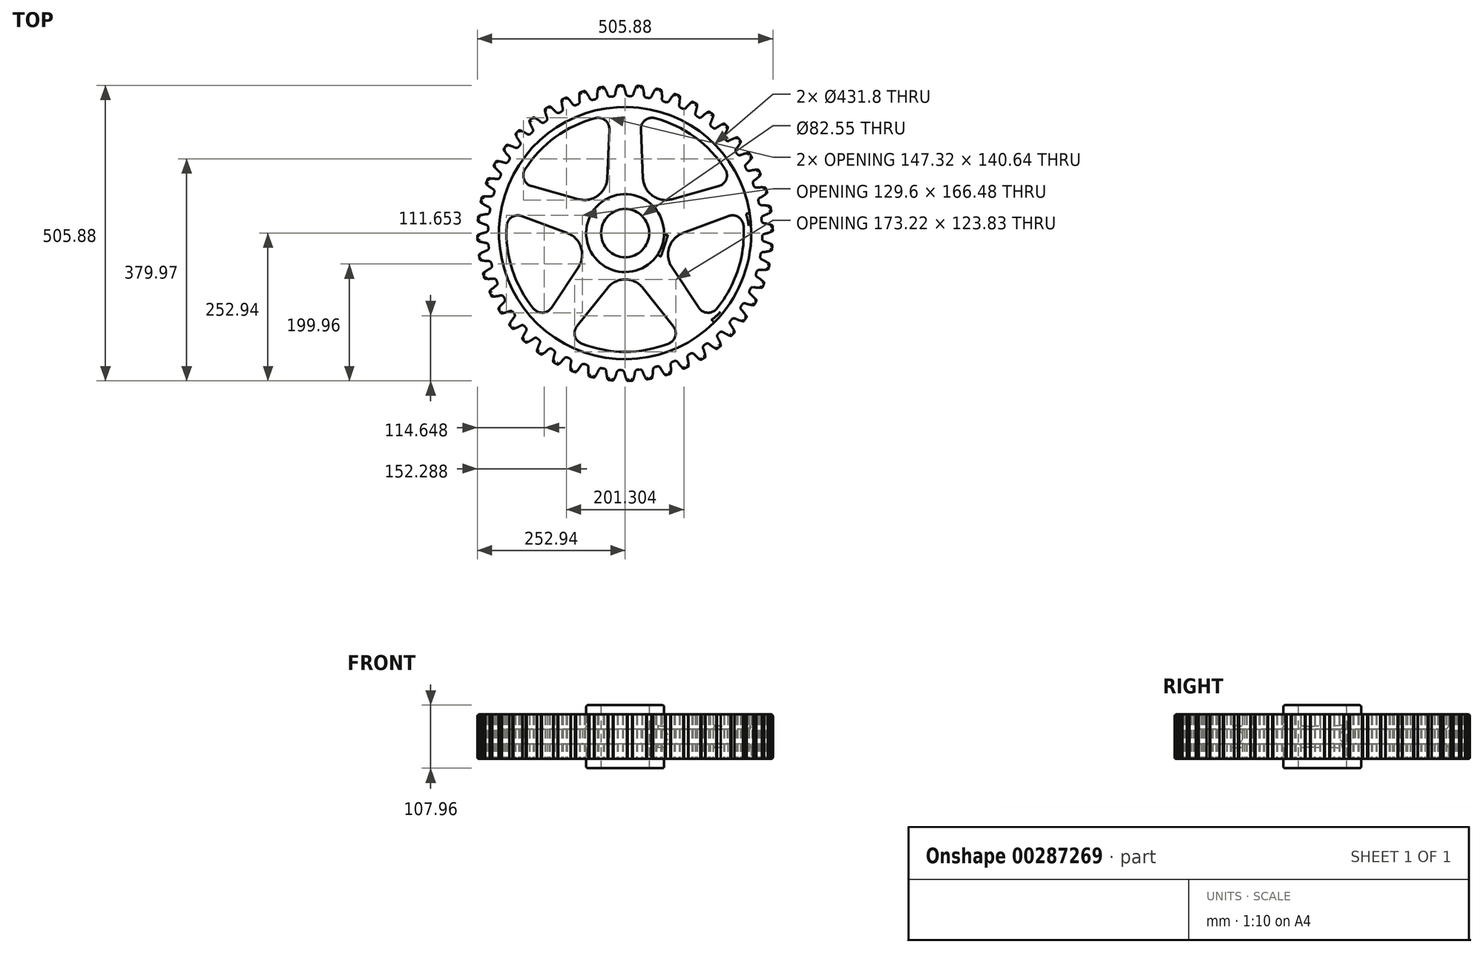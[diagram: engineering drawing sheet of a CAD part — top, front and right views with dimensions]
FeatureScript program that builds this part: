
annotation { "Feature Type Name" : "Feature", "Feature Type Description" : "" }
export const myFeature = defineFeature(function(context is Context, id is Id, definition is map)
    precondition{}
    {
        {
            var Q0;
            Q0=qCreatedBy(makeId("Top.planeOp"),FACE);
            var sketch = newSketch(context, id + "F0", { "sketchPlane" : qUnion([Q0])});
            skCircle(sketch, "E0", {"center": v(0, 0) * mm, "radius": 215.9 * mm});
            skCircle(sketch, "E1", {"center": v(0, 0) * mm, "radius": 233.95 * mm, "construction": true});
            skCircle(sketch, "E2", {"center": v(0, 0) * mm, "radius": 243.84 * mm, "construction": true});
            skLineSegment(sketch, "E3", {"start": v(0, 0) * mm, "end": v(0, 296.8) * mm, "construction": true});
            skLineSegment(sketch, "E4", {"start": v(0, 0) * mm, "end": v(-9.72, 296.8) * mm, "construction": true});
            skLineSegment(sketch, "E5", {"start": v(0, 243.84) * mm, "end": v(-159.16, 238.63) * mm, "construction": true});
            skLineSegment(sketch, "E6", {"start": v(0, 243.84) * mm, "end": v(-157.2, 197.65) * mm, "construction": true});
            skArc(sketch, "E7", {"start": v(-21.3, 233.73) * mm, "mid": v(7.68, -234.57) * mm, "end": v(5.96, 234.62) * mm});
            skCircle(sketch, "E8", {"center": v(0, 243.84) * mm, "radius": 60.96 * mm, "construction": true});
            skArc(sketch, "E9", {"start": v(1.3, 238.54) * mm, "mid": v(-0.65, 245.9) * mm, "end": v(-3.5, 252.96) * mm});
            skArc(sketch, "E10.MirrorCS", {"start": v(-16.9, 237.95) * mm, "mid": v(-15.44, 245.42) * mm, "end": v(-13.06, 252.65) * mm});
            skArc(sketch, "E11.trimOffspring", {"start": v(-3.5, 252.96) * mm, "mid": v(-8.28, 252.85) * mm, "end": v(-13.06, 252.65) * mm});
            skPoint(sketch, "E12.visualSharp", {"position": v(-17.29, 234.06) * mm});
            skArc(sketch, "E12.filletArc", {"start": v(-21.3, 233.73) * mm, "mid": v(-18.36, 235.07) * mm, "end": v(-16.9, 237.95) * mm});
            skPoint(sketch, "E13.visualSharp", {"position": v(1.94, 234.69) * mm});
            skArc(sketch, "E13.filletArc", {"start": v(1.3, 238.54) * mm, "mid": v(2.94, 235.77) * mm, "end": v(5.96, 234.62) * mm});
            skCircle(sketch, "E14", {"center": v(0, 0) * mm, "radius": 41.28 * mm});
            skCircle(sketch, "E15", {"center": v(0, 0) * mm, "radius": 66.68 * mm});
            skSolve(sketch);
        }
        {
            var Q0;
            Q0 = qSketchRegion(id + "F0", true);
            extrude(context, id + "F1", {"entities" : qUnion([Q0]), "depth" : 76.2 * mm, "symmetric" : true});
        }
        {
            var Q0;
            Q0=makeQuery(id+"F1.opExtrude","SWEPT_EDGE",EDGE,{"disambiguationData":[OSD([sQuery(id+"F0.wireOp",EDGE,"a425b38e-6d31-48f0-aded-03e86b7642bf0.MirrorCS"),sQuery(id+"F0.wireOp",EDGE,"e7ba85ad-8bea-4f75-aefd-55836ceef68a.trimOffspring")])]});
            var Q1;
            Q1=makeQuery(id+"F1.opExtrude","SWEPT_EDGE",EDGE,{"disambiguationData":[OSD([sQuery(id+"F0.wireOp",EDGE,"58a562a5-3fed-4315-ace1-1cd0f613343d.trimOffspring"),sQuery(id+"F0.wireOp",EDGE,"e7ba85ad-8bea-4f75-aefd-55836ceef68a.trimOffspring")])]});
            var Q2;
            Q2=makeQuery(id+"F1.opExtrude","SWEPT_EDGE",EDGE,{"disambiguationData":[OSD([sQuery(id+"F0.wireOp",EDGE,"E10.MirrorCS"),sQuery(id+"F0.wireOp",EDGE,"E11.trimOffspring")])]});
            var Q3;
            Q3=makeQuery(id+"F1.opExtrude","SWEPT_EDGE",EDGE,{"disambiguationData":[OSD([sQuery(id+"F0.wireOp",EDGE,"E9"),sQuery(id+"F0.wireOp",EDGE,"E11.trimOffspring")])]});
            chamfer(context, id + "F2", {"entities" : qUnion([Q0, Q1, Q2, Q3]), "width" : 1.59 * mm, "tangentPropagation" : true});
        }
        {
            var Q0;
            Q0=makeQuery(id+"F0.imprint","IMPRINT",FACE,{"disambiguationData":[TD([[makeQuery(id+"F0.imprint","IMPRINT",EDGE,{"derivedFrom":sQuery(id+"F0.wireOp",EDGE,"E14")}),-1.0]])]});
            extrude(context, id + "F3", {"entities" : qUnion([Q0]), "depth" : 107.95 * mm, "symmetric" : true});
        }
        {
            var Q0;
            Q0=makeQuery(id+"F1.opExtrude","SWEPT_BODY",BODY,{"disambiguationData":[OSD([sQuery(id+"F0.wireOp",EDGE,"E0"),sQuery(id+"F0.wireOp",EDGE,"E7"),sQuery(id+"F0.wireOp",EDGE,"E9"),sQuery(id+"F0.wireOp",EDGE,"E10.MirrorCS"),sQuery(id+"F0.wireOp",EDGE,"E11.trimOffspring"),sQuery(id+"F0.wireOp",EDGE,"E12.filletArc"),sQuery(id+"F0.wireOp",EDGE,"E13.filletArc")])]});
            var Q1;
            Q1=makeQuery(id+"F3.opExtrude","SWEPT_FACE",FACE,{"disambiguationData":[OSD([sQuery(id+"F0.wireOp",EDGE,"E15")])]});
            circularPattern(context, id + "F4", {"operationType" : NewBodyOperationType.ADD, "entities" : qUnion([Q0]), "axis" : qUnion([Q1]), "angle" : 360 * degree, "instanceCount" : 48, "equalSpace" : true});
        }
        {
            var Q0;
            Q0=qCreatedBy(makeId("Front.planeOp"),FACE);
            var sketch = newSketch(context, id + "F5", { "sketchPlane" : qUnion([Q0])});
            skLineSegment(sketch, "E16", {"start": v(-215.9, -12.7) * mm, "end": v(-215.9, 12.7) * mm});
            skPoint(sketch, "E17.orphan", {"position": v(-215.9, 38.1) * mm});
            skPoint(sketch, "E18.orphan", {"position": v(-215.9, -38.1) * mm});
            skLineSegment(sketch, "E19", {"start": v(-66.68, -12.7) * mm, "end": v(-66.68, 12.7) * mm});
            skLineSegment(sketch, "E20.bottom", {"start": v(-66.68, -12.7) * mm, "end": v(-79.38, -12.7) * mm});
            skLineSegment(sketch, "E20.top", {"start": v(-66.68, 12.7) * mm, "end": v(-79.38, 12.7) * mm});
            skLineSegment(sketch, "E20.right", {"start": v(-79.38, -12.7) * mm, "end": v(-79.38, 12.7) * mm});
            skPoint(sketch, "E20.middle", {"position": v(-66.68, 0) * mm});
            skPoint(sketch, "E20.left.end.orphan", {"position": v(-53.98, 12.7) * mm});
            skPoint(sketch, "E20.left.start.orphan", {"position": v(-53.98, -12.7) * mm});
            skPoint(sketch, "E21.orphan", {"position": v(-66.68, -53.98) * mm});
            skPoint(sketch, "E22.orphan", {"position": v(-66.68, 53.98) * mm});
            skLineSegment(sketch, "E23.bottom", {"start": v(-203.2, 12.7) * mm, "end": v(-215.9, 12.7) * mm});
            skLineSegment(sketch, "E23.top", {"start": v(-203.2, -12.7) * mm, "end": v(-215.9, -12.7) * mm});
            skLineSegment(sketch, "E23.left", {"start": v(-203.2, 12.7) * mm, "end": v(-203.2, -12.7) * mm});
            skPoint(sketch, "E23.middle", {"position": v(-215.9, 0) * mm});
            skPoint(sketch, "E23.right.start.orphan", {"position": v(-228.6, 12.7) * mm});
            skPoint(sketch, "E24.orphan", {"position": v(-228.6, -12.7) * mm});
            skSolve(sketch);
        }
        {
            var Q0;
            Q0=makeQuery(id+"F5.imprint","IMPRINT",FACE,{"disambiguationData":[TD([[makeQuery(id+"F5.imprint","IMPRINT",EDGE,{"derivedFrom":sQuery(id+"F5.wireOp",EDGE,"E16")}),-1.0]])]});
            var Q1;
            Q1=makeQuery(id+"F3.opExtrude","SWEPT_FACE",FACE,{"disambiguationData":[OSD([sQuery(id+"F0.wireOp",EDGE,"E14")])]});
            revolve(context, id + "F6", {"operationType" : NewBodyOperationType.ADD, "entities" : qUnion([Q0]), "axis" : qUnion([Q1]), "revolveType" : RevolveType.FULL});
        }
        {
            var Q0;
            Q0=makeQuery(id+"F5.imprint","IMPRINT",FACE,{"disambiguationData":[TD([[makeQuery(id+"F5.imprint","IMPRINT",EDGE,{"derivedFrom":sQuery(id+"F5.wireOp",EDGE,"E19")}),1.0]])]});
            var Q1;
            Q1=makeQuery(id+"F3.opExtrude","SWEPT_FACE",FACE,{"disambiguationData":[OSD([sQuery(id+"F0.wireOp",EDGE,"E14")])]});
            revolve(context, id + "F7", {"operationType" : NewBodyOperationType.ADD, "entities" : qUnion([Q0]), "axis" : qUnion([Q1]), "revolveType" : RevolveType.FULL});
        }
        {
            var Q0;
            Q0=qCreatedBy(makeId("Top.planeOp"),FACE);
            var sketch = newSketch(context, id + "F8", { "sketchPlane" : qUnion([Q0])});
            skCircle(sketch, "E25.0", {"center": v(0, 0) * mm, "radius": 215.9 * mm});
            skCircle(sketch, "E26.0", {"center": v(0, 0) * mm, "radius": 66.68 * mm});
            skLineSegment(sketch, "E27", {"start": v(0, 66.68) * mm, "end": v(0, 215.9) * mm});
            skLineSegment(sketch, "E28", {"start": v(25.4, 214.4) * mm, "end": v(32.14, 58.42) * mm});
            skLineSegment(sketch, "E29.MirrorCS", {"start": v(-25.4, 214.4) * mm, "end": v(-32.14, 58.42) * mm});
            skSolve(sketch);
        }
        {
            var Q0;
            {var subQ0=sQuery(id+"F8.wireOp",EDGE,"E27");Q0=makeQuery(id+"F8.imprint","IMPRINT",FACE,{"disambiguationData":[TD([[makeQuery(id+"F8.imprint","IMPRINT",EDGE,{"derivedFrom":subQ0}),1.0]])]});}
            var Q1;
            {var subQ0=sQuery(id+"F8.wireOp",EDGE,"E27");Q1=makeQuery(id+"F8.imprint","IMPRINT",FACE,{"disambiguationData":[TD([[makeQuery(id+"F8.imprint","IMPRINT",EDGE,{"derivedFrom":subQ0}),-1.0]])]});}
            extrude(context, id + "F9", {"entities" : qUnion([Q0, Q1]), "depth" : 25.4 * mm, "symmetric" : true});
        }
        {
            var Q0;
            Q0=makeQuery(id+"F9.opExtrude","SWEPT_BODY",BODY,{"disambiguationData":[OSD([sQuery(id+"F8.wireOp",EDGE,"E25.0"),sQuery(id+"F8.wireOp",EDGE,"E26.0"),sQuery(id+"F8.wireOp",EDGE,"E28"),sQuery(id+"F8.wireOp",EDGE,"E29.MirrorCS")])]});
            var Q1;
            Q1=makeQuery(id+"F3.opExtrude","SWEPT_FACE",FACE,{"disambiguationData":[OSD([sQuery(id+"F0.wireOp",EDGE,"E14")])]});
            circularPattern(context, id + "F10", {"entities" : qUnion([Q0]), "axis" : qUnion([Q1]), "angle" : 360 * degree, "instanceCount" : 5, "equalSpace" : true});
        }
        {
            var Q0;
            Q0=makeQuery(id+"F10.opPattern","COPY",BODY,{"derivedFrom":makeQuery(id+"F9.opExtrude","SWEPT_BODY",BODY,{"disambiguationData":[OSD([sQuery(id+"F8.wireOp",EDGE,"E25.0"),sQuery(id+"F8.wireOp",EDGE,"E26.0"),sQuery(id+"F8.wireOp",EDGE,"E28"),sQuery(id+"F8.wireOp",EDGE,"E29.MirrorCS")])]}),"instanceName":"2"});
            var Q1;
            Q1=makeQuery(id+"F10.opPattern","COPY",BODY,{"derivedFrom":makeQuery(id+"F9.opExtrude","SWEPT_BODY",BODY,{"disambiguationData":[OSD([sQuery(id+"F8.wireOp",EDGE,"E25.0"),sQuery(id+"F8.wireOp",EDGE,"E26.0"),sQuery(id+"F8.wireOp",EDGE,"E28"),sQuery(id+"F8.wireOp",EDGE,"E29.MirrorCS")])]}),"instanceName":"1"});
            var Q2;
            Q2=makeQuery(id+"F10.opPattern","COPY",BODY,{"derivedFrom":makeQuery(id+"F9.opExtrude","SWEPT_BODY",BODY,{"disambiguationData":[OSD([sQuery(id+"F8.wireOp",EDGE,"E25.0"),sQuery(id+"F8.wireOp",EDGE,"E26.0"),sQuery(id+"F8.wireOp",EDGE,"E28"),sQuery(id+"F8.wireOp",EDGE,"E29.MirrorCS")])]}),"instanceName":"4"});
            var Q3;
            Q3=makeQuery(id+"F10.opPattern","COPY",BODY,{"derivedFrom":makeQuery(id+"F9.opExtrude","SWEPT_BODY",BODY,{"disambiguationData":[OSD([sQuery(id+"F8.wireOp",EDGE,"E25.0"),sQuery(id+"F8.wireOp",EDGE,"E26.0"),sQuery(id+"F8.wireOp",EDGE,"E28"),sQuery(id+"F8.wireOp",EDGE,"E29.MirrorCS")])]}),"instanceName":"3"});
            var Q4;
            Q4=makeQuery(id+"F9.opExtrude","SWEPT_BODY",BODY,{"disambiguationData":[OSD([sQuery(id+"F8.wireOp",EDGE,"E25.0"),sQuery(id+"F8.wireOp",EDGE,"E26.0"),sQuery(id+"F8.wireOp",EDGE,"E28"),sQuery(id+"F8.wireOp",EDGE,"E29.MirrorCS")])]});
            var Q5;
            Q5=makeQuery(id+"F3.opExtrude","SWEPT_BODY",BODY,{"disambiguationData":[OSD([sQuery(id+"F0.wireOp",EDGE,"E14"),sQuery(id+"F0.wireOp",EDGE,"E15")])]});
            var Q6;
            Q6=makeQuery(id+"F1.opExtrude","SWEPT_BODY",BODY,{"disambiguationData":[OSD([sQuery(id+"F0.wireOp",EDGE,"E0"),sQuery(id+"F0.wireOp",EDGE,"E7"),sQuery(id+"F0.wireOp",EDGE,"E9"),sQuery(id+"F0.wireOp",EDGE,"E10.MirrorCS"),sQuery(id+"F0.wireOp",EDGE,"E11.trimOffspring"),sQuery(id+"F0.wireOp",EDGE,"E12.filletArc"),sQuery(id+"F0.wireOp",EDGE,"E13.filletArc")])]});
            booleanBodies(context, id + "F11", {"operationType" : BooleanOperationType.UNION, "tools" : qUnion([Q0, Q1, Q2, Q3, Q4, Q5, Q6])});
        }
        {
            var Q0;
            Q0=makeQuery(id+"F11.opBoolean","INTERSECT",EDGE,{"derivedFrom":[makeQuery(id+"F7.opRevolve","SWEPT_FACE",FACE,{"disambiguationData":[OSD([sQuery(id+"F5.wireOp",EDGE,"E20.right")])]}),makeQuery(id+"F9.opExtrude","SWEPT_FACE",FACE,{"disambiguationData":[OSD([sQuery(id+"F8.wireOp",EDGE,"E28")])]})]});
            var Q1;
            Q1=makeQuery(id+"F11.opBoolean","INTERSECT",EDGE,{"derivedFrom":[makeQuery(id+"F7.opRevolve","SWEPT_FACE",FACE,{"disambiguationData":[OSD([sQuery(id+"F5.wireOp",EDGE,"E20.right")])]}),makeQuery(id+"F10.opPattern","COPY",FACE,{"derivedFrom":makeQuery(id+"F9.opExtrude","SWEPT_FACE",FACE,{"disambiguationData":[OSD([sQuery(id+"F8.wireOp",EDGE,"E29.MirrorCS")])]}),"instanceName":"4"})]});
            var Q2;
            Q2=makeQuery(id+"F11.opBoolean","INTERSECT",EDGE,{"derivedFrom":[makeQuery(id+"F7.opRevolve","SWEPT_FACE",FACE,{"disambiguationData":[OSD([sQuery(id+"F5.wireOp",EDGE,"E20.right")])]}),makeQuery(id+"F10.opPattern","COPY",FACE,{"derivedFrom":makeQuery(id+"F9.opExtrude","SWEPT_FACE",FACE,{"disambiguationData":[OSD([sQuery(id+"F8.wireOp",EDGE,"E28")])]}),"instanceName":"1"})]});
            var Q3;
            Q3=makeQuery(id+"F11.opBoolean","INTERSECT",EDGE,{"derivedFrom":[makeQuery(id+"F7.opRevolve","SWEPT_FACE",FACE,{"disambiguationData":[OSD([sQuery(id+"F5.wireOp",EDGE,"E20.right")])]}),makeQuery(id+"F9.opExtrude","SWEPT_FACE",FACE,{"disambiguationData":[OSD([sQuery(id+"F8.wireOp",EDGE,"E29.MirrorCS")])]})]});
            var Q4;
            Q4=makeQuery(id+"F11.opBoolean","INTERSECT",EDGE,{"derivedFrom":[makeQuery(id+"F7.opRevolve","SWEPT_FACE",FACE,{"disambiguationData":[OSD([sQuery(id+"F5.wireOp",EDGE,"E20.right")])]}),makeQuery(id+"F10.opPattern","COPY",FACE,{"derivedFrom":makeQuery(id+"F9.opExtrude","SWEPT_FACE",FACE,{"disambiguationData":[OSD([sQuery(id+"F8.wireOp",EDGE,"E29.MirrorCS")])]}),"instanceName":"1"})]});
            var Q5;
            Q5=makeQuery(id+"F11.opBoolean","INTERSECT",EDGE,{"derivedFrom":[makeQuery(id+"F7.opRevolve","SWEPT_FACE",FACE,{"disambiguationData":[OSD([sQuery(id+"F5.wireOp",EDGE,"E20.right")])]}),makeQuery(id+"F10.opPattern","COPY",FACE,{"derivedFrom":makeQuery(id+"F9.opExtrude","SWEPT_FACE",FACE,{"disambiguationData":[OSD([sQuery(id+"F8.wireOp",EDGE,"E28")])]}),"instanceName":"2"})]});
            var Q6;
            Q6=makeQuery(id+"F11.opBoolean","INTERSECT",EDGE,{"derivedFrom":[makeQuery(id+"F7.opRevolve","SWEPT_FACE",FACE,{"disambiguationData":[OSD([sQuery(id+"F5.wireOp",EDGE,"E20.right")])]}),makeQuery(id+"F10.opPattern","COPY",FACE,{"derivedFrom":makeQuery(id+"F9.opExtrude","SWEPT_FACE",FACE,{"disambiguationData":[OSD([sQuery(id+"F8.wireOp",EDGE,"E29.MirrorCS")])]}),"instanceName":"2"})]});
            var Q7;
            Q7=makeQuery(id+"F11.opBoolean","INTERSECT",EDGE,{"derivedFrom":[makeQuery(id+"F7.opRevolve","SWEPT_FACE",FACE,{"disambiguationData":[OSD([sQuery(id+"F5.wireOp",EDGE,"E20.right")])]}),makeQuery(id+"F10.opPattern","COPY",FACE,{"derivedFrom":makeQuery(id+"F9.opExtrude","SWEPT_FACE",FACE,{"disambiguationData":[OSD([sQuery(id+"F8.wireOp",EDGE,"E28")])]}),"instanceName":"3"})]});
            var Q8;
            Q8=makeQuery(id+"F11.opBoolean","INTERSECT",EDGE,{"derivedFrom":[makeQuery(id+"F7.opRevolve","SWEPT_FACE",FACE,{"disambiguationData":[OSD([sQuery(id+"F5.wireOp",EDGE,"E20.right")])]}),makeQuery(id+"F10.opPattern","COPY",FACE,{"derivedFrom":makeQuery(id+"F9.opExtrude","SWEPT_FACE",FACE,{"disambiguationData":[OSD([sQuery(id+"F8.wireOp",EDGE,"E29.MirrorCS")])]}),"instanceName":"3"})]});
            var Q9;
            Q9=makeQuery(id+"F11.opBoolean","INTERSECT",EDGE,{"derivedFrom":[makeQuery(id+"F7.opRevolve","SWEPT_FACE",FACE,{"disambiguationData":[OSD([sQuery(id+"F5.wireOp",EDGE,"E20.right")])]}),makeQuery(id+"F10.opPattern","COPY",FACE,{"derivedFrom":makeQuery(id+"F9.opExtrude","SWEPT_FACE",FACE,{"disambiguationData":[OSD([sQuery(id+"F8.wireOp",EDGE,"E28")])]}),"instanceName":"4"})]});
            fillet(context, id + "F12", {"entities" : qUnion([Q0, Q1, Q2, Q3, Q4, Q5, Q6, Q7, Q8, Q9]), "radius" : 38.1 * mm, "tangentPropagation" : true, "allowEdgeOverflow" : false});
        }
        {
            var Q0;
            Q0=makeQuery(id+"F11.opBoolean","INTERSECT",EDGE,{"derivedFrom":[makeQuery(id+"F6.opRevolve","SWEPT_FACE",FACE,{"disambiguationData":[OSD([sQuery(id+"F5.wireOp",EDGE,"E23.left")])]}),makeQuery(id+"F10.opPattern","COPY",FACE,{"derivedFrom":makeQuery(id+"F9.opExtrude","SWEPT_FACE",FACE,{"disambiguationData":[OSD([sQuery(id+"F8.wireOp",EDGE,"E28")])]}),"instanceName":"2"})]});
            var Q1;
            Q1=makeQuery(id+"F11.opBoolean","INTERSECT",EDGE,{"derivedFrom":[makeQuery(id+"F6.opRevolve","SWEPT_FACE",FACE,{"disambiguationData":[OSD([sQuery(id+"F5.wireOp",EDGE,"E23.left")])]}),makeQuery(id+"F10.opPattern","COPY",FACE,{"derivedFrom":makeQuery(id+"F9.opExtrude","SWEPT_FACE",FACE,{"disambiguationData":[OSD([sQuery(id+"F8.wireOp",EDGE,"E29.MirrorCS")])]}),"instanceName":"2"})]});
            var Q2;
            Q2=makeQuery(id+"F11.opBoolean","INTERSECT",EDGE,{"derivedFrom":[makeQuery(id+"F6.opRevolve","SWEPT_FACE",FACE,{"disambiguationData":[OSD([sQuery(id+"F5.wireOp",EDGE,"E23.left")])]}),makeQuery(id+"F10.opPattern","COPY",FACE,{"derivedFrom":makeQuery(id+"F9.opExtrude","SWEPT_FACE",FACE,{"disambiguationData":[OSD([sQuery(id+"F8.wireOp",EDGE,"E28")])]}),"instanceName":"3"})]});
            var Q3;
            Q3=makeQuery(id+"F11.opBoolean","INTERSECT",EDGE,{"derivedFrom":[makeQuery(id+"F6.opRevolve","SWEPT_FACE",FACE,{"disambiguationData":[OSD([sQuery(id+"F5.wireOp",EDGE,"E23.left")])]}),makeQuery(id+"F10.opPattern","COPY",FACE,{"derivedFrom":makeQuery(id+"F9.opExtrude","SWEPT_FACE",FACE,{"disambiguationData":[OSD([sQuery(id+"F8.wireOp",EDGE,"E29.MirrorCS")])]}),"instanceName":"3"})]});
            var Q4;
            Q4=makeQuery(id+"F11.opBoolean","INTERSECT",EDGE,{"derivedFrom":[makeQuery(id+"F6.opRevolve","SWEPT_FACE",FACE,{"disambiguationData":[OSD([sQuery(id+"F5.wireOp",EDGE,"E23.left")])]}),makeQuery(id+"F10.opPattern","COPY",FACE,{"derivedFrom":makeQuery(id+"F9.opExtrude","SWEPT_FACE",FACE,{"disambiguationData":[OSD([sQuery(id+"F8.wireOp",EDGE,"E29.MirrorCS")])]}),"instanceName":"1"})]});
            var Q5;
            Q5=makeQuery(id+"F11.opBoolean","INTERSECT",EDGE,{"derivedFrom":[makeQuery(id+"F6.opRevolve","SWEPT_FACE",FACE,{"disambiguationData":[OSD([sQuery(id+"F5.wireOp",EDGE,"E23.left")])]}),makeQuery(id+"F10.opPattern","COPY",FACE,{"derivedFrom":makeQuery(id+"F9.opExtrude","SWEPT_FACE",FACE,{"disambiguationData":[OSD([sQuery(id+"F8.wireOp",EDGE,"E28")])]}),"instanceName":"1"})]});
            var Q6;
            Q6=makeQuery(id+"F11.opBoolean","INTERSECT",EDGE,{"derivedFrom":[makeQuery(id+"F6.opRevolve","SWEPT_FACE",FACE,{"disambiguationData":[OSD([sQuery(id+"F5.wireOp",EDGE,"E23.left")])]}),makeQuery(id+"F10.opPattern","COPY",FACE,{"derivedFrom":makeQuery(id+"F9.opExtrude","SWEPT_FACE",FACE,{"disambiguationData":[OSD([sQuery(id+"F8.wireOp",EDGE,"E28")])]}),"instanceName":"4"})]});
            var Q7;
            Q7=makeQuery(id+"F11.opBoolean","INTERSECT",EDGE,{"derivedFrom":[makeQuery(id+"F6.opRevolve","SWEPT_FACE",FACE,{"disambiguationData":[OSD([sQuery(id+"F5.wireOp",EDGE,"E23.left")])]}),makeQuery(id+"F10.opPattern","COPY",FACE,{"derivedFrom":makeQuery(id+"F9.opExtrude","SWEPT_FACE",FACE,{"disambiguationData":[OSD([sQuery(id+"F8.wireOp",EDGE,"E29.MirrorCS")])]}),"instanceName":"4"})]});
            var Q8;
            Q8=makeQuery(id+"F11.opBoolean","INTERSECT",EDGE,{"derivedFrom":[makeQuery(id+"F6.opRevolve","SWEPT_FACE",FACE,{"disambiguationData":[OSD([sQuery(id+"F5.wireOp",EDGE,"E23.left")])]}),makeQuery(id+"F9.opExtrude","SWEPT_FACE",FACE,{"disambiguationData":[OSD([sQuery(id+"F8.wireOp",EDGE,"E28")])]})]});
            var Q9;
            Q9=makeQuery(id+"F11.opBoolean","INTERSECT",EDGE,{"derivedFrom":[makeQuery(id+"F6.opRevolve","SWEPT_FACE",FACE,{"disambiguationData":[OSD([sQuery(id+"F5.wireOp",EDGE,"E23.left")])]}),makeQuery(id+"F9.opExtrude","SWEPT_FACE",FACE,{"disambiguationData":[OSD([sQuery(id+"F8.wireOp",EDGE,"E29.MirrorCS")])]})]});
            fillet(context, id + "F13", {"entities" : qUnion([Q0, Q1, Q2, Q3, Q4, Q5, Q6, Q7, Q8, Q9]), "radius" : 19.05 * mm, "tangentPropagation" : true, "allowEdgeOverflow" : false});
        }
        {
            var Q0;
            {var subQ0=sQuery(id+"F8.wireOp",EDGE,"E29.MirrorCS");var subQ3=sQuery(id+"F5.wireOp",EDGE,"E23.left");var subQ4=sQuery(id+"F5.wireOp",EDGE,"E23.bottom");Q0=makeQuery(id+"F11.opBoolean","SPLIT",EDGE,{"disambiguationData":[TD([makeQuery(id+"F10.opPattern","COPY",FACE,{"derivedFrom":makeQuery(id+"F9.opExtrude","SWEPT_FACE",FACE,{"disambiguationData":[OSD([subQ0])]}),"instanceName":"2"})])],"derivedFrom":makeQuery(id+"F6.opRevolve","SWEPT_EDGE",EDGE,{"disambiguationData":[OSD([subQ4,subQ3])]})});}
            var Q1;
            {var subQ0=sQuery(id+"F8.wireOp",EDGE,"E29.MirrorCS");var subQ3=sQuery(id+"F5.wireOp",EDGE,"E23.left");var subQ4=sQuery(id+"F5.wireOp",EDGE,"E23.bottom");Q1=makeQuery(id+"F11.opBoolean","SPLIT",EDGE,{"disambiguationData":[TD([makeQuery(id+"F10.opPattern","COPY",FACE,{"derivedFrom":makeQuery(id+"F9.opExtrude","SWEPT_FACE",FACE,{"disambiguationData":[OSD([subQ0])]}),"instanceName":"1"})])],"derivedFrom":makeQuery(id+"F6.opRevolve","SWEPT_EDGE",EDGE,{"disambiguationData":[OSD([subQ4,subQ3])]})});}
            var Q2;
            {var subQ0=sQuery(id+"F8.wireOp",EDGE,"E29.MirrorCS");var subQ3=sQuery(id+"F5.wireOp",EDGE,"E23.left");var subQ4=sQuery(id+"F5.wireOp",EDGE,"E23.bottom");Q2=makeQuery(id+"F11.opBoolean","SPLIT",EDGE,{"disambiguationData":[TD([makeQuery(id+"F10.opPattern","COPY",FACE,{"derivedFrom":makeQuery(id+"F9.opExtrude","SWEPT_FACE",FACE,{"disambiguationData":[OSD([subQ0])]}),"instanceName":"3"})])],"derivedFrom":makeQuery(id+"F6.opRevolve","SWEPT_EDGE",EDGE,{"disambiguationData":[OSD([subQ4,subQ3])]})});}
            var Q3;
            {var subQ1=sQuery(id+"F8.wireOp",EDGE,"E28");var subQ3=sQuery(id+"F5.wireOp",EDGE,"E23.left");var subQ4=sQuery(id+"F5.wireOp",EDGE,"E23.bottom");Q3=makeQuery(id+"F11.opBoolean","SPLIT",EDGE,{"disambiguationData":[TD([makeQuery(id+"F9.opExtrude","SWEPT_FACE",FACE,{"disambiguationData":[OSD([subQ1])]})])],"derivedFrom":makeQuery(id+"F6.opRevolve","SWEPT_EDGE",EDGE,{"disambiguationData":[OSD([subQ4,subQ3])]})});}
            var Q4;
            {var subQ1=sQuery(id+"F8.wireOp",EDGE,"E29.MirrorCS");var subQ3=sQuery(id+"F5.wireOp",EDGE,"E23.left");var subQ4=sQuery(id+"F5.wireOp",EDGE,"E23.bottom");Q4=makeQuery(id+"F11.opBoolean","SPLIT",EDGE,{"disambiguationData":[TD([makeQuery(id+"F9.opExtrude","SWEPT_FACE",FACE,{"disambiguationData":[OSD([subQ1])]})])],"derivedFrom":makeQuery(id+"F6.opRevolve","SWEPT_EDGE",EDGE,{"disambiguationData":[OSD([subQ4,subQ3])]})});}
            var Q5;
            {var subQ0=sQuery(id+"F5.wireOp",EDGE,"E23.left");var subQ1=sQuery(id+"F8.wireOp",EDGE,"E29.MirrorCS");var subQ4=sQuery(id+"F5.wireOp",EDGE,"E23.top");Q5=makeQuery(id+"F11.opBoolean","SPLIT",EDGE,{"disambiguationData":[TD([makeQuery(id+"F9.opExtrude","SWEPT_FACE",FACE,{"disambiguationData":[OSD([subQ1])]})])],"derivedFrom":makeQuery(id+"F6.opRevolve","SWEPT_EDGE",EDGE,{"disambiguationData":[OSD([subQ4,subQ0])]})});}
            var Q6;
            {var subQ0=sQuery(id+"F5.wireOp",EDGE,"E23.left");var subQ2=sQuery(id+"F8.wireOp",EDGE,"E28");var subQ4=sQuery(id+"F5.wireOp",EDGE,"E23.top");Q6=makeQuery(id+"F11.opBoolean","SPLIT",EDGE,{"disambiguationData":[TD([makeQuery(id+"F9.opExtrude","SWEPT_FACE",FACE,{"disambiguationData":[OSD([subQ2])]})])],"derivedFrom":makeQuery(id+"F6.opRevolve","SWEPT_EDGE",EDGE,{"disambiguationData":[OSD([subQ4,subQ0])]})});}
            var Q7;
            {var subQ0=sQuery(id+"F5.wireOp",EDGE,"E23.left");var subQ1=sQuery(id+"F8.wireOp",EDGE,"E29.MirrorCS");var subQ4=sQuery(id+"F5.wireOp",EDGE,"E23.top");Q7=makeQuery(id+"F11.opBoolean","SPLIT",EDGE,{"disambiguationData":[TD([makeQuery(id+"F10.opPattern","COPY",FACE,{"derivedFrom":makeQuery(id+"F9.opExtrude","SWEPT_FACE",FACE,{"disambiguationData":[OSD([subQ1])]}),"instanceName":"1"})])],"derivedFrom":makeQuery(id+"F6.opRevolve","SWEPT_EDGE",EDGE,{"disambiguationData":[OSD([subQ4,subQ0])]})});}
            var Q8;
            {var subQ0=sQuery(id+"F5.wireOp",EDGE,"E23.left");var subQ1=sQuery(id+"F8.wireOp",EDGE,"E29.MirrorCS");var subQ4=sQuery(id+"F5.wireOp",EDGE,"E23.top");Q8=makeQuery(id+"F11.opBoolean","SPLIT",EDGE,{"disambiguationData":[TD([makeQuery(id+"F10.opPattern","COPY",FACE,{"derivedFrom":makeQuery(id+"F9.opExtrude","SWEPT_FACE",FACE,{"disambiguationData":[OSD([subQ1])]}),"instanceName":"2"})])],"derivedFrom":makeQuery(id+"F6.opRevolve","SWEPT_EDGE",EDGE,{"disambiguationData":[OSD([subQ4,subQ0])]})});}
            var Q9;
            {var subQ0=sQuery(id+"F5.wireOp",EDGE,"E23.left");var subQ1=sQuery(id+"F8.wireOp",EDGE,"E29.MirrorCS");var subQ4=sQuery(id+"F5.wireOp",EDGE,"E23.top");Q9=makeQuery(id+"F11.opBoolean","SPLIT",EDGE,{"disambiguationData":[TD([makeQuery(id+"F10.opPattern","COPY",FACE,{"derivedFrom":makeQuery(id+"F9.opExtrude","SWEPT_FACE",FACE,{"disambiguationData":[OSD([subQ1])]}),"instanceName":"3"})])],"derivedFrom":makeQuery(id+"F6.opRevolve","SWEPT_EDGE",EDGE,{"disambiguationData":[OSD([subQ4,subQ0])]})});}
            fillet(context, id + "F14", {"entities" : qUnion([Q0, Q1, Q2, Q3, Q4, Q5, Q6, Q7, Q8, Q9]), "radius" : 12.7 * mm, "tangentPropagation" : true, "allowEdgeOverflow" : false});
        }
        {
            var Q0;
            {var subQ0=sQuery(id+"F0.wireOp",EDGE,"E0");var subQ3=sQuery(id+"F5.wireOp",EDGE,"E23.top");var subQ4=makeQuery(id+"F6.opRevolve","SWEPT_FACE",FACE,{"disambiguationData":[OSD([subQ3])]});var subQ5=sQuery(id+"F5.wireOp",EDGE,"E23.left");var subQ6=sQuery(id+"F8.wireOp",EDGE,"E29.MirrorCS");Q0=makeQuery(id+"F14.opFillet","BLEND_EDGE",EDGE,{"blendedFrom":[makeQuery(id+"F11.opBoolean","SPLIT",EDGE,{"disambiguationData":[TD([makeQuery(id+"F10.opPattern","COPY",FACE,{"derivedFrom":makeQuery(id+"F9.opExtrude","SWEPT_FACE",FACE,{"disambiguationData":[OSD([subQ6])]}),"instanceName":"3"})])],"derivedFrom":makeQuery(id+"F6.opRevolve","SWEPT_EDGE",EDGE,{"disambiguationData":[OSD([subQ3,subQ5])]})}),makeQuery(id+"F6.boolean.opBoolean","SPLIT",FACE,{"disambiguationData":[TD([subQ4])],"derivedFrom":makeQuery(id+"F1.opExtrude","SWEPT_FACE",FACE,{"disambiguationData":[OSD([subQ0])]})})],"blendedInto":[makeQuery(id+"F6.boolean.opBoolean","SPLIT",FACE,{"disambiguationData":[TD([subQ4])],"derivedFrom":makeQuery(id+"F1.opExtrude","SWEPT_FACE",FACE,{"disambiguationData":[OSD([subQ0])]})})]});}
            var Q1;
            {var subQ0=makeQuery(id+"F9.opExtrude","CAP_EDGE",EDGE,{"disambiguationData":[OSD([sQuery(id+"F8.wireOp",EDGE,"E26.0")])],"isStart":true});Q1=makeQuery(id+"F11.opBoolean","MERGE",EDGE,{"derivedFrom":[makeQuery(id+"F7.opRevolve","SWEPT_EDGE",EDGE,{"disambiguationData":[OSD([sQuery(id+"F5.wireOp",EDGE,"E19"),sQuery(id+"F5.wireOp",EDGE,"E20.bottom")])]}),subQ0,makeQuery(id+"F10.opPattern","COPY",EDGE,{"derivedFrom":subQ0,"instanceName":"1"}),makeQuery(id+"F10.opPattern","COPY",EDGE,{"derivedFrom":subQ0,"instanceName":"2"}),makeQuery(id+"F10.opPattern","COPY",EDGE,{"derivedFrom":subQ0,"instanceName":"3"}),makeQuery(id+"F10.opPattern","COPY",EDGE,{"derivedFrom":subQ0,"instanceName":"4"})]});}
            var Q2;
            {var subQ0=makeQuery(id+"F9.opExtrude","CAP_EDGE",EDGE,{"disambiguationData":[OSD([sQuery(id+"F8.wireOp",EDGE,"E26.0")])],"isStart":false});Q2=makeQuery(id+"F11.opBoolean","MERGE",EDGE,{"derivedFrom":[makeQuery(id+"F7.opRevolve","SWEPT_EDGE",EDGE,{"disambiguationData":[OSD([sQuery(id+"F5.wireOp",EDGE,"E19"),sQuery(id+"F5.wireOp",EDGE,"E20.top")])]}),subQ0,makeQuery(id+"F10.opPattern","COPY",EDGE,{"derivedFrom":subQ0,"instanceName":"1"}),makeQuery(id+"F10.opPattern","COPY",EDGE,{"derivedFrom":subQ0,"instanceName":"2"}),makeQuery(id+"F10.opPattern","COPY",EDGE,{"derivedFrom":subQ0,"instanceName":"3"}),makeQuery(id+"F10.opPattern","COPY",EDGE,{"derivedFrom":subQ0,"instanceName":"4"})]});}
            var Q3;
            {var subQ0=makeQuery(id+"F9.opExtrude","CAP_EDGE",EDGE,{"disambiguationData":[OSD([sQuery(id+"F8.wireOp",EDGE,"E25.0")])],"isStart":false});Q3=makeQuery(id+"F11.opBoolean","MERGE",EDGE,{"derivedFrom":[makeQuery(id+"F6.opRevolve","SWEPT_EDGE",EDGE,{"disambiguationData":[OSD([sQuery(id+"F5.wireOp",EDGE,"E16"),sQuery(id+"F5.wireOp",EDGE,"E23.bottom")])]}),subQ0,makeQuery(id+"F10.opPattern","COPY",EDGE,{"derivedFrom":subQ0,"instanceName":"1"}),makeQuery(id+"F10.opPattern","COPY",EDGE,{"derivedFrom":subQ0,"instanceName":"2"}),makeQuery(id+"F10.opPattern","COPY",EDGE,{"derivedFrom":subQ0,"instanceName":"3"}),makeQuery(id+"F10.opPattern","COPY",EDGE,{"derivedFrom":subQ0,"instanceName":"4"})]});}
            fillet(context, id + "F15", {"entities" : qUnion([Q0, Q1, Q2, Q3]), "radius" : 6.35 * mm, "tangentPropagation" : true, "allowEdgeOverflow" : false});
        }
        {
            var Q0;
            {var subQ0=makeQuery(id+"F1.opExtrude","CAP_FACE",FACE,{"disambiguationData":[OSD([sQuery(id+"F0.wireOp",EDGE,"E0"),sQuery(id+"F0.wireOp",EDGE,"E7"),sQuery(id+"F0.wireOp",EDGE,"E9"),sQuery(id+"F0.wireOp",EDGE,"E10.MirrorCS"),sQuery(id+"F0.wireOp",EDGE,"E11.trimOffspring"),sQuery(id+"F0.wireOp",EDGE,"E12.filletArc"),sQuery(id+"F0.wireOp",EDGE,"E13.filletArc")])],"isStart":false});Q0=makeQuery(id+"F4.boolean.opBoolean","MERGE",FACE,{"derivedFrom":[subQ0,makeQuery(id+"F4.opPattern","COPY",FACE,{"derivedFrom":subQ0,"instanceName":"1"}),makeQuery(id+"F4.opPattern","COPY",FACE,{"derivedFrom":subQ0,"instanceName":"2"}),makeQuery(id+"F4.opPattern","COPY",FACE,{"derivedFrom":subQ0,"instanceName":"3"}),makeQuery(id+"F4.opPattern","COPY",FACE,{"derivedFrom":subQ0,"instanceName":"4"}),makeQuery(id+"F4.opPattern","COPY",FACE,{"derivedFrom":subQ0,"instanceName":"5"}),makeQuery(id+"F4.opPattern","COPY",FACE,{"derivedFrom":subQ0,"instanceName":"6"}),makeQuery(id+"F4.opPattern","COPY",FACE,{"derivedFrom":subQ0,"instanceName":"7"}),makeQuery(id+"F4.opPattern","COPY",FACE,{"derivedFrom":subQ0,"instanceName":"8"}),makeQuery(id+"F4.opPattern","COPY",FACE,{"derivedFrom":subQ0,"instanceName":"9"}),makeQuery(id+"F4.opPattern","COPY",FACE,{"derivedFrom":subQ0,"instanceName":"10"}),makeQuery(id+"F4.opPattern","COPY",FACE,{"derivedFrom":subQ0,"instanceName":"11"}),makeQuery(id+"F4.opPattern","COPY",FACE,{"derivedFrom":subQ0,"instanceName":"12"}),makeQuery(id+"F4.opPattern","COPY",FACE,{"derivedFrom":subQ0,"instanceName":"13"}),makeQuery(id+"F4.opPattern","COPY",FACE,{"derivedFrom":subQ0,"instanceName":"14"}),makeQuery(id+"F4.opPattern","COPY",FACE,{"derivedFrom":subQ0,"instanceName":"15"}),makeQuery(id+"F4.opPattern","COPY",FACE,{"derivedFrom":subQ0,"instanceName":"16"}),makeQuery(id+"F4.opPattern","COPY",FACE,{"derivedFrom":subQ0,"instanceName":"17"}),makeQuery(id+"F4.opPattern","COPY",FACE,{"derivedFrom":subQ0,"instanceName":"18"}),makeQuery(id+"F4.opPattern","COPY",FACE,{"derivedFrom":subQ0,"instanceName":"19"}),makeQuery(id+"F4.opPattern","COPY",FACE,{"derivedFrom":subQ0,"instanceName":"20"}),makeQuery(id+"F4.opPattern","COPY",FACE,{"derivedFrom":subQ0,"instanceName":"21"}),makeQuery(id+"F4.opPattern","COPY",FACE,{"derivedFrom":subQ0,"instanceName":"22"}),makeQuery(id+"F4.opPattern","COPY",FACE,{"derivedFrom":subQ0,"instanceName":"23"}),makeQuery(id+"F4.opPattern","COPY",FACE,{"derivedFrom":subQ0,"instanceName":"24"}),makeQuery(id+"F4.opPattern","COPY",FACE,{"derivedFrom":subQ0,"instanceName":"25"}),makeQuery(id+"F4.opPattern","COPY",FACE,{"derivedFrom":subQ0,"instanceName":"26"}),makeQuery(id+"F4.opPattern","COPY",FACE,{"derivedFrom":subQ0,"instanceName":"27"}),makeQuery(id+"F4.opPattern","COPY",FACE,{"derivedFrom":subQ0,"instanceName":"28"}),makeQuery(id+"F4.opPattern","COPY",FACE,{"derivedFrom":subQ0,"instanceName":"29"}),makeQuery(id+"F4.opPattern","COPY",FACE,{"derivedFrom":subQ0,"instanceName":"30"}),makeQuery(id+"F4.opPattern","COPY",FACE,{"derivedFrom":subQ0,"instanceName":"31"}),makeQuery(id+"F4.opPattern","COPY",FACE,{"derivedFrom":subQ0,"instanceName":"32"}),makeQuery(id+"F4.opPattern","COPY",FACE,{"derivedFrom":subQ0,"instanceName":"33"}),makeQuery(id+"F4.opPattern","COPY",FACE,{"derivedFrom":subQ0,"instanceName":"34"}),makeQuery(id+"F4.opPattern","COPY",FACE,{"derivedFrom":subQ0,"instanceName":"35"}),makeQuery(id+"F4.opPattern","COPY",FACE,{"derivedFrom":subQ0,"instanceName":"36"}),makeQuery(id+"F4.opPattern","COPY",FACE,{"derivedFrom":subQ0,"instanceName":"37"}),makeQuery(id+"F4.opPattern","COPY",FACE,{"derivedFrom":subQ0,"instanceName":"38"}),makeQuery(id+"F4.opPattern","COPY",FACE,{"derivedFrom":subQ0,"instanceName":"39"}),makeQuery(id+"F4.opPattern","COPY",FACE,{"derivedFrom":subQ0,"instanceName":"40"}),makeQuery(id+"F4.opPattern","COPY",FACE,{"derivedFrom":subQ0,"instanceName":"41"}),makeQuery(id+"F4.opPattern","COPY",FACE,{"derivedFrom":subQ0,"instanceName":"42"}),makeQuery(id+"F4.opPattern","COPY",FACE,{"derivedFrom":subQ0,"instanceName":"43"}),makeQuery(id+"F4.opPattern","COPY",FACE,{"derivedFrom":subQ0,"instanceName":"44"}),makeQuery(id+"F4.opPattern","COPY",FACE,{"derivedFrom":subQ0,"instanceName":"45"}),makeQuery(id+"F4.opPattern","COPY",FACE,{"derivedFrom":subQ0,"instanceName":"46"}),makeQuery(id+"F4.opPattern","COPY",FACE,{"derivedFrom":subQ0,"instanceName":"47"})]});}
            var Q1;
            Q1=makeQuery(id+"F3.opExtrude","CAP_EDGE",EDGE,{"disambiguationData":[OSD([sQuery(id+"F0.wireOp",EDGE,"E14")])],"isStart":false});
            var Q2;
            Q2=makeQuery(id+"F3.opExtrude","CAP_EDGE",EDGE,{"disambiguationData":[OSD([sQuery(id+"F0.wireOp",EDGE,"E15")])],"isStart":false});
            var Q3;
            {var subQ0=makeQuery(id+"F1.opExtrude","CAP_FACE",FACE,{"disambiguationData":[OSD([sQuery(id+"F0.wireOp",EDGE,"E0"),sQuery(id+"F0.wireOp",EDGE,"E7"),sQuery(id+"F0.wireOp",EDGE,"E9"),sQuery(id+"F0.wireOp",EDGE,"E10.MirrorCS"),sQuery(id+"F0.wireOp",EDGE,"E11.trimOffspring"),sQuery(id+"F0.wireOp",EDGE,"E12.filletArc"),sQuery(id+"F0.wireOp",EDGE,"E13.filletArc")])],"isStart":true});Q3=makeQuery(id+"F4.boolean.opBoolean","MERGE",FACE,{"derivedFrom":[subQ0,makeQuery(id+"F4.opPattern","COPY",FACE,{"derivedFrom":subQ0,"instanceName":"1"}),makeQuery(id+"F4.opPattern","COPY",FACE,{"derivedFrom":subQ0,"instanceName":"2"}),makeQuery(id+"F4.opPattern","COPY",FACE,{"derivedFrom":subQ0,"instanceName":"3"}),makeQuery(id+"F4.opPattern","COPY",FACE,{"derivedFrom":subQ0,"instanceName":"4"}),makeQuery(id+"F4.opPattern","COPY",FACE,{"derivedFrom":subQ0,"instanceName":"5"}),makeQuery(id+"F4.opPattern","COPY",FACE,{"derivedFrom":subQ0,"instanceName":"6"}),makeQuery(id+"F4.opPattern","COPY",FACE,{"derivedFrom":subQ0,"instanceName":"7"}),makeQuery(id+"F4.opPattern","COPY",FACE,{"derivedFrom":subQ0,"instanceName":"8"}),makeQuery(id+"F4.opPattern","COPY",FACE,{"derivedFrom":subQ0,"instanceName":"9"}),makeQuery(id+"F4.opPattern","COPY",FACE,{"derivedFrom":subQ0,"instanceName":"10"}),makeQuery(id+"F4.opPattern","COPY",FACE,{"derivedFrom":subQ0,"instanceName":"11"}),makeQuery(id+"F4.opPattern","COPY",FACE,{"derivedFrom":subQ0,"instanceName":"12"}),makeQuery(id+"F4.opPattern","COPY",FACE,{"derivedFrom":subQ0,"instanceName":"13"}),makeQuery(id+"F4.opPattern","COPY",FACE,{"derivedFrom":subQ0,"instanceName":"14"}),makeQuery(id+"F4.opPattern","COPY",FACE,{"derivedFrom":subQ0,"instanceName":"15"}),makeQuery(id+"F4.opPattern","COPY",FACE,{"derivedFrom":subQ0,"instanceName":"16"}),makeQuery(id+"F4.opPattern","COPY",FACE,{"derivedFrom":subQ0,"instanceName":"17"}),makeQuery(id+"F4.opPattern","COPY",FACE,{"derivedFrom":subQ0,"instanceName":"18"}),makeQuery(id+"F4.opPattern","COPY",FACE,{"derivedFrom":subQ0,"instanceName":"19"}),makeQuery(id+"F4.opPattern","COPY",FACE,{"derivedFrom":subQ0,"instanceName":"20"}),makeQuery(id+"F4.opPattern","COPY",FACE,{"derivedFrom":subQ0,"instanceName":"21"}),makeQuery(id+"F4.opPattern","COPY",FACE,{"derivedFrom":subQ0,"instanceName":"22"}),makeQuery(id+"F4.opPattern","COPY",FACE,{"derivedFrom":subQ0,"instanceName":"23"}),makeQuery(id+"F4.opPattern","COPY",FACE,{"derivedFrom":subQ0,"instanceName":"24"}),makeQuery(id+"F4.opPattern","COPY",FACE,{"derivedFrom":subQ0,"instanceName":"25"}),makeQuery(id+"F4.opPattern","COPY",FACE,{"derivedFrom":subQ0,"instanceName":"26"}),makeQuery(id+"F4.opPattern","COPY",FACE,{"derivedFrom":subQ0,"instanceName":"27"}),makeQuery(id+"F4.opPattern","COPY",FACE,{"derivedFrom":subQ0,"instanceName":"28"}),makeQuery(id+"F4.opPattern","COPY",FACE,{"derivedFrom":subQ0,"instanceName":"29"}),makeQuery(id+"F4.opPattern","COPY",FACE,{"derivedFrom":subQ0,"instanceName":"30"}),makeQuery(id+"F4.opPattern","COPY",FACE,{"derivedFrom":subQ0,"instanceName":"31"}),makeQuery(id+"F4.opPattern","COPY",FACE,{"derivedFrom":subQ0,"instanceName":"32"}),makeQuery(id+"F4.opPattern","COPY",FACE,{"derivedFrom":subQ0,"instanceName":"33"}),makeQuery(id+"F4.opPattern","COPY",FACE,{"derivedFrom":subQ0,"instanceName":"34"}),makeQuery(id+"F4.opPattern","COPY",FACE,{"derivedFrom":subQ0,"instanceName":"35"}),makeQuery(id+"F4.opPattern","COPY",FACE,{"derivedFrom":subQ0,"instanceName":"36"}),makeQuery(id+"F4.opPattern","COPY",FACE,{"derivedFrom":subQ0,"instanceName":"37"}),makeQuery(id+"F4.opPattern","COPY",FACE,{"derivedFrom":subQ0,"instanceName":"38"}),makeQuery(id+"F4.opPattern","COPY",FACE,{"derivedFrom":subQ0,"instanceName":"39"}),makeQuery(id+"F4.opPattern","COPY",FACE,{"derivedFrom":subQ0,"instanceName":"40"}),makeQuery(id+"F4.opPattern","COPY",FACE,{"derivedFrom":subQ0,"instanceName":"41"}),makeQuery(id+"F4.opPattern","COPY",FACE,{"derivedFrom":subQ0,"instanceName":"42"}),makeQuery(id+"F4.opPattern","COPY",FACE,{"derivedFrom":subQ0,"instanceName":"43"}),makeQuery(id+"F4.opPattern","COPY",FACE,{"derivedFrom":subQ0,"instanceName":"44"}),makeQuery(id+"F4.opPattern","COPY",FACE,{"derivedFrom":subQ0,"instanceName":"45"}),makeQuery(id+"F4.opPattern","COPY",FACE,{"derivedFrom":subQ0,"instanceName":"46"}),makeQuery(id+"F4.opPattern","COPY",FACE,{"derivedFrom":subQ0,"instanceName":"47"})]});}
            var Q4;
            Q4=makeQuery(id+"F3.opExtrude","CAP_FACE",FACE,{"disambiguationData":[OSD([sQuery(id+"F0.wireOp",EDGE,"E14"),sQuery(id+"F0.wireOp",EDGE,"E15")])],"isStart":true});
            fillet(context, id + "F16", {"entities" : qUnion([Q0, Q1, Q2, Q3, Q4]), "radius" : 3.17 * mm, "tangentPropagation" : true, "allowEdgeOverflow" : false});
        }
    });
